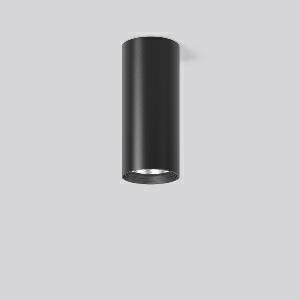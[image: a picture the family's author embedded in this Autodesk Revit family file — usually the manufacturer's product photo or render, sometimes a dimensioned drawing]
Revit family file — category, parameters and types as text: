
# Revit family: heledon_mini_a_931209_003_3_76_217d
name_source: partatom
category: Lighting Fixtures
units: mm (PartAtom-declared; Revit-internal decimal feet)

## family parameters
Cut with Voids When Loaded = No
Host = Face
Light Source = No
Part Type = Normal
Room Calculation Point = No
Round Connector Dimension = Use Diameter
Shared = No

## types (1)
- HELEDON mini A (1 x LED Modul 935, 3600 lm, 3500)
    Apparent Load = 29 VA
    Approval mark = CE
    CIE Flux Codes = 99 100 100 100 100
    Color Rendering = 92
    Color Temperature = 3500
    Default Elevation = 1800 mm
    Description = Series: HELEDON mini
Cylindrical surface-mounted downlight. Housing: die-cast aluminium, powder-coated. Internal ceiling frame polycarbonate with bayonet mounting. Black plastic ring and recessed LED to prevent glare from the side. Optical assembly with reflector made of MIRO-Silver with 98% total light reflection for outstanding efficiency - can be changed without tools. Best colour rendering index Ra>90. Suitable for Ceiling mounting. Easy installation with a separate ceiling frame with bayonet mounting and plug connection. Driver integrated. Connected via plug-in connector. High quality converter without flickering and stroboscopic effect. The following accessories can be mounted without use of tools: interchangeable lenses, decorative glasses, honeycomb louvre, clear and frosted diffusers, white interchangeable plastic ring. 
Colour: deep black, matt (RAL 9005)
Diameter: 87 mm
Height: 197 mm
Lamp: LED
Socket: without socket
Colour temperature: 3500K
Colour rendering index (CRI): 92
System power: 29 W
Rated luminous flux: 3600 lm
Luminous efficiency: 124 lm/W
Control gear: Converter, dimmable, DALI
Protection class: I
Type of protection: IP 20
    Height = 197 mm
    Lamp = 1 x LED Modul 935
    Lamp Light Flux = 3600 lm
    Lamp count = 1
    Length = 87 mm
    Lifetime = 50000 h
    Luminous efficacy = 124 lm/W
    Manufacturer = RZB
    ModVariant = No
    Model = 931209.003.3.76
    Mounting Place = Ceiling
    Mounting Type = Surface mounted
    Number of Poles = 1
    OnlyDefault = Yes
    Power Factor = 1
    Product Name = HELEDON mini A
    Product group = Surface mounted downlights
    ProductGroupID = 302
    Protection Class = Protection class I
    Protection Degree = IP 20
    RLX_Detail_Level = 1
    RLX_Emergency_Light_Flux = 0 lm
    RLX_Emergency_Type = 0
    RLX_Emergency_Type_DB = No
    RlxData = <blob elided: 107181 chars, md5=d9eb7caa>
    Socket = socket
    Standby Power = 0 W
    System Light Flux = 3600 lm
    System Power = 29 W
    Type Comments = Product without accessories
    Type Image = 931188.003.jpg
    URL = http://relux.com
    VarID = ---
    Voltage = 230 V
    Voltage Range = 220-240 V
    Weight = 0.00 kg
    Width = 0 mm  [stored 0 ft]

note: [stored X ft] marks values corroborated as IEEE doubles in the binary element streams (Revit-internal decimal feet)

## geometry (parser evidence)
native form markers: Blend x4, Sweep x10
no freeform markers — native parametric forms only
